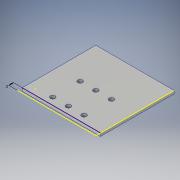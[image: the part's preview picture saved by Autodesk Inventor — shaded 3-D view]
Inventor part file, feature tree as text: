
AUTODESK INVENTOR PART (.ipt)
format: ipt  version: 2019 (Build 230136000, 136)  size: 138,752 bytes
history: native  units: mm
features: sketch x4, extrude x2, other x1, hole x1
ambient origin geometry x8: Origin, YZ Plane, XZ Plane, XY Plane, X Axis, Y Axis, Z Axis, Center Point
bodies: Body1 (feature_tree), Body2 (feature_tree)
feature tree (8):
  other  "ソリッド1"
  extrude  "押し出し1"  Depth=50.0mm
  hole  "穴1"  [1 undecoded]
  sketch  "スケッチ3"
  extrude  "押し出し2"  Depth=2.0mm TaperAngle=0.0deg
  sketch  "スケッチ1"
  sketch  "スケッチ2"
  sketch  "スケッチ4"
note: 1 required parameter value undecoded (feature->parameter linkage not recoverable at this tier; creation-order binding heuristic only, values carry confidence <= 0.55)
